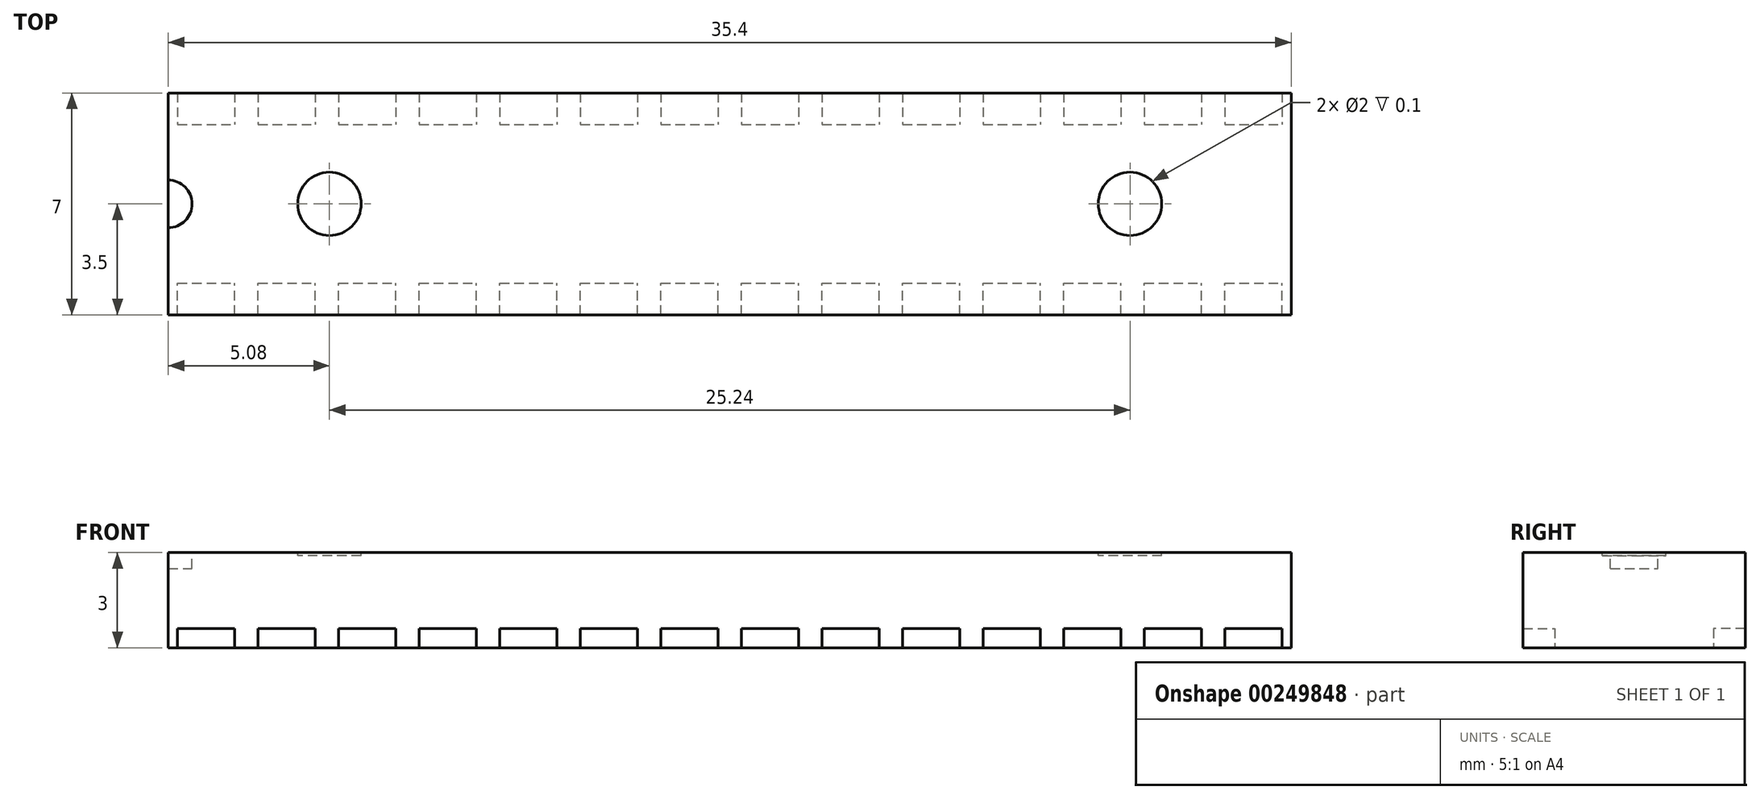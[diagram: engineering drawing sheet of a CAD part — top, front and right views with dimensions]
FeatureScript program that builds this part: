
annotation { "Feature Type Name" : "Feature", "Feature Type Description" : "" }
export const myFeature = defineFeature(function(context is Context, id is Id, definition is map)
    precondition{}
    {
        {
            var Q0;
            Q0=qCreatedBy(makeId("Top.planeOp"),FACE);
            var sketch = newSketch(context, id + "F0", { "sketchPlane" : qUnion([Q0])});
            skLineSegment(sketch, "E0.bottom", {"start": v(0, 0) * mm, "end": v(35.4, 0) * mm});
            skLineSegment(sketch, "E0.top", {"start": v(0, 7) * mm, "end": v(35.4, 7) * mm});
            skLineSegment(sketch, "E0.left", {"start": v(0, 0) * mm, "end": v(0, 7) * mm});
            skLineSegment(sketch, "E0.right", {"start": v(35.4, 0) * mm, "end": v(35.4, 7) * mm});
            skSolve(sketch);
        }
        {
            var Q0;
            Q0 = qSketchRegion(id + "F0", true);
            extrude(context, id + "F1", {"entities" : qUnion([Q0]), "depth" : 3 * mm});
        }
        {
            var Q0;
            Q0=makeQuery(id+"F1.opExtrude","CAP_FACE",FACE,{"disambiguationData":[OSD([sQuery(id+"F0.wireOp",EDGE,"E0.bottom"),sQuery(id+"F0.wireOp",EDGE,"E0.top"),sQuery(id+"F0.wireOp",EDGE,"E0.left"),sQuery(id+"F0.wireOp",EDGE,"E0.right")])],"isStart":true});
            var sketch = newSketch(context, id + "F2", { "sketchPlane" : qUnion([Q0])});
            skLineSegment(sketch, "E1", {"start": v(17.7, 0) * mm, "end": v(17.7, -7) * mm, "construction": true});
            skLineSegment(sketch, "E2.bottom", {"start": v(15.53, 0) * mm, "end": v(17.33, 0) * mm});
            skLineSegment(sketch, "E2.top", {"start": v(15.53, -1) * mm, "end": v(17.33, -1) * mm});
            skLineSegment(sketch, "E2.left", {"start": v(15.53, 0) * mm, "end": v(15.53, -1) * mm});
            skLineSegment(sketch, "E2.right", {"start": v(17.33, 0) * mm, "end": v(17.33, -1) * mm});
            skLineSegment(sketch, "E3.1.0.0", {"start": v(18.07, 0) * mm, "end": v(18.07, -1) * mm});
            skLineSegment(sketch, "E3.1.0.1", {"start": v(18.07, 0) * mm, "end": v(19.87, 0) * mm});
            skLineSegment(sketch, "E3.1.0.2", {"start": v(18.07, -1) * mm, "end": v(19.87, -1) * mm});
            skLineSegment(sketch, "E3.1.0.3", {"start": v(19.87, 0) * mm, "end": v(19.87, -1) * mm});
            skLineSegment(sketch, "E3.2.0.0", {"start": v(20.61, 0) * mm, "end": v(20.61, -1) * mm});
            skLineSegment(sketch, "E3.2.0.1", {"start": v(20.61, 0) * mm, "end": v(22.41, 0) * mm});
            skLineSegment(sketch, "E3.2.0.2", {"start": v(20.61, -1) * mm, "end": v(22.41, -1) * mm});
            skLineSegment(sketch, "E3.2.0.3", {"start": v(22.41, 0) * mm, "end": v(22.41, -1) * mm});
            skLineSegment(sketch, "E3.3.0.0", {"start": v(23.15, 0) * mm, "end": v(23.15, -1) * mm});
            skLineSegment(sketch, "E3.3.0.1", {"start": v(23.15, 0) * mm, "end": v(24.95, 0) * mm});
            skLineSegment(sketch, "E3.3.0.2", {"start": v(23.15, -1) * mm, "end": v(24.95, -1) * mm});
            skLineSegment(sketch, "E3.3.0.3", {"start": v(24.95, 0) * mm, "end": v(24.95, -1) * mm});
            skLineSegment(sketch, "E3.4.0.0", {"start": v(25.7, 0) * mm, "end": v(25.7, -1) * mm});
            skLineSegment(sketch, "E3.4.0.1", {"start": v(25.7, 0) * mm, "end": v(27.5, 0) * mm});
            skLineSegment(sketch, "E3.4.0.2", {"start": v(25.7, -1) * mm, "end": v(27.5, -1) * mm});
            skLineSegment(sketch, "E3.4.0.3", {"start": v(27.5, 0) * mm, "end": v(27.5, -1) * mm});
            skLineSegment(sketch, "E3.5.0.0", {"start": v(28.23, 0) * mm, "end": v(28.23, -1) * mm});
            skLineSegment(sketch, "E3.5.0.1", {"start": v(28.23, 0) * mm, "end": v(30.03, 0) * mm});
            skLineSegment(sketch, "E3.5.0.2", {"start": v(28.23, -1) * mm, "end": v(30.03, -1) * mm});
            skLineSegment(sketch, "E3.5.0.3", {"start": v(30.03, 0) * mm, "end": v(30.03, -1) * mm});
            skLineSegment(sketch, "E3.6.0.0", {"start": v(30.77, 0) * mm, "end": v(30.77, -1) * mm});
            skLineSegment(sketch, "E3.6.0.1", {"start": v(30.77, 0) * mm, "end": v(32.57, 0) * mm});
            skLineSegment(sketch, "E3.6.0.2", {"start": v(30.77, -1) * mm, "end": v(32.57, -1) * mm});
            skLineSegment(sketch, "E3.6.0.3", {"start": v(32.57, 0) * mm, "end": v(32.57, -1) * mm});
            skLineSegment(sketch, "E3.7.0.0", {"start": v(33.31, 0) * mm, "end": v(33.31, -1) * mm});
            skLineSegment(sketch, "E3.7.0.1", {"start": v(33.31, 0) * mm, "end": v(35.1, 0) * mm});
            skLineSegment(sketch, "E3.7.0.2", {"start": v(33.31, -1) * mm, "end": v(35.1, -1) * mm});
            skLineSegment(sketch, "E3.7.0.3", {"start": v(35.1, 0) * mm, "end": v(35.1, -1) * mm});
            skLineSegment(sketch, "E3.direction1", {"start": v(15.53, -1) * mm, "end": v(18.07, -1) * mm, "construction": true});
            skLineSegment(sketch, "E4.1.0.0", {"start": v(14.8, 0) * mm, "end": v(14.8, -1) * mm});
            skLineSegment(sketch, "E4.1.0.1", {"start": v(13, 0) * mm, "end": v(13, -1) * mm});
            skLineSegment(sketch, "E4.1.0.2", {"start": v(13, 0) * mm, "end": v(14.8, 0) * mm});
            skLineSegment(sketch, "E4.2.0.0", {"start": v(12.25, 0) * mm, "end": v(12.25, -1) * mm});
            skLineSegment(sketch, "E4.2.0.1", {"start": v(10.45, 0) * mm, "end": v(10.45, -1) * mm});
            skLineSegment(sketch, "E4.2.0.2", {"start": v(10.45, 0) * mm, "end": v(12.25, 0) * mm});
            skLineSegment(sketch, "E4.3.0.0", {"start": v(9.7, 0) * mm, "end": v(9.7, -1) * mm});
            skLineSegment(sketch, "E4.3.0.1", {"start": v(7.9, 0) * mm, "end": v(7.9, -1) * mm});
            skLineSegment(sketch, "E4.3.0.2", {"start": v(7.9, 0) * mm, "end": v(9.7, 0) * mm});
            skLineSegment(sketch, "E4.4.0.0", {"start": v(7.17, 0) * mm, "end": v(7.17, -1) * mm});
            skLineSegment(sketch, "E4.4.0.1", {"start": v(5.37, 0) * mm, "end": v(5.37, -1) * mm});
            skLineSegment(sketch, "E4.4.0.2", {"start": v(5.37, 0) * mm, "end": v(7.17, 0) * mm});
            skLineSegment(sketch, "E4.5.0.0", {"start": v(4.63, 0) * mm, "end": v(4.63, -1) * mm});
            skLineSegment(sketch, "E4.5.0.1", {"start": v(2.83, 0) * mm, "end": v(2.83, -1) * mm});
            skLineSegment(sketch, "E4.5.0.2", {"start": v(2.83, 0) * mm, "end": v(4.63, 0) * mm});
            skLineSegment(sketch, "E4.6.0.0", {"start": v(2.09, 0) * mm, "end": v(2.09, -1) * mm});
            skLineSegment(sketch, "E4.6.0.1", {"start": v(0.29, 0) * mm, "end": v(0.29, -1) * mm});
            skLineSegment(sketch, "E4.6.0.2", {"start": v(0.29, 0) * mm, "end": v(2.09, 0) * mm});
            skLineSegment(sketch, "E4.direction1", {"start": v(17.33, -1) * mm, "end": v(14.8, -1) * mm, "construction": true});
            skLineSegment(sketch, "E5", {"start": v(0.29, -1) * mm, "end": v(2.09, -1) * mm});
            skLineSegment(sketch, "E6", {"start": v(2.83, -1) * mm, "end": v(4.63, -1) * mm});
            skLineSegment(sketch, "E7", {"start": v(5.37, -1) * mm, "end": v(7.17, -1) * mm});
            skLineSegment(sketch, "E8", {"start": v(7.9, -1) * mm, "end": v(9.7, -1) * mm});
            skLineSegment(sketch, "E9", {"start": v(10.45, -1) * mm, "end": v(12.25, -1) * mm});
            skLineSegment(sketch, "E10", {"start": v(13, -1) * mm, "end": v(14.8, -1) * mm});
            skLineSegment(sketch, "E11", {"start": v(0, -3.5) * mm, "end": v(35.4, -3.5) * mm, "construction": true});
            skLineSegment(sketch, "E12.MirrorCS", {"start": v(2.09, -7) * mm, "end": v(2.09, -6) * mm});
            skLineSegment(sketch, "E13.MirrorCS", {"start": v(0.29, -7) * mm, "end": v(2.09, -7) * mm});
            skLineSegment(sketch, "E14.MirrorCS", {"start": v(0.29, -6) * mm, "end": v(2.09, -6) * mm});
            skLineSegment(sketch, "E15.MirrorCS", {"start": v(0.29, -7) * mm, "end": v(0.29, -6) * mm});
            skLineSegment(sketch, "E16.MirrorCS", {"start": v(14.8, -7) * mm, "end": v(14.8, -6) * mm});
            skLineSegment(sketch, "E17.MirrorCS", {"start": v(15.53, -6) * mm, "end": v(17.33, -6) * mm});
            skLineSegment(sketch, "E18.MirrorCS", {"start": v(7.17, -7) * mm, "end": v(7.17, -6) * mm});
            skLineSegment(sketch, "E19.MirrorCS", {"start": v(13, -7) * mm, "end": v(14.8, -7) * mm});
            skLineSegment(sketch, "E20.MirrorCS", {"start": v(2.83, -6) * mm, "end": v(4.63, -6) * mm});
            skLineSegment(sketch, "E21.MirrorCS", {"start": v(2.83, -7) * mm, "end": v(4.63, -7) * mm});
            skLineSegment(sketch, "E22.MirrorCS", {"start": v(5.37, -6) * mm, "end": v(7.17, -6) * mm});
            skLineSegment(sketch, "E23.MirrorCS", {"start": v(10.45, -7) * mm, "end": v(12.25, -7) * mm});
            skLineSegment(sketch, "E24.MirrorCS", {"start": v(17.33, -6) * mm, "end": v(14.8, -6) * mm, "construction": true});
            skLineSegment(sketch, "E25.MirrorCS", {"start": v(5.37, -7) * mm, "end": v(7.17, -7) * mm});
            skLineSegment(sketch, "E26.MirrorCS", {"start": v(5.37, -7) * mm, "end": v(5.37, -6) * mm});
            skLineSegment(sketch, "E27.MirrorCS", {"start": v(12.25, -7) * mm, "end": v(12.25, -6) * mm});
            skLineSegment(sketch, "E28.MirrorCS", {"start": v(7.9, -6) * mm, "end": v(9.7, -6) * mm});
            skLineSegment(sketch, "E29.MirrorCS", {"start": v(9.7, -7) * mm, "end": v(9.7, -6) * mm});
            skLineSegment(sketch, "E30.MirrorCS", {"start": v(4.63, -7) * mm, "end": v(4.63, -6) * mm});
            skLineSegment(sketch, "E31.MirrorCS", {"start": v(13, -6) * mm, "end": v(14.8, -6) * mm});
            skLineSegment(sketch, "E32.MirrorCS", {"start": v(13, -7) * mm, "end": v(13, -6) * mm});
            skLineSegment(sketch, "E33.MirrorCS", {"start": v(7.9, -7) * mm, "end": v(9.7, -7) * mm});
            skLineSegment(sketch, "E34.MirrorCS", {"start": v(2.83, -7) * mm, "end": v(2.83, -6) * mm});
            skLineSegment(sketch, "E35.MirrorCS", {"start": v(10.45, -7) * mm, "end": v(10.45, -6) * mm});
            skLineSegment(sketch, "E36.MirrorCS", {"start": v(7.9, -7) * mm, "end": v(7.9, -6) * mm});
            skLineSegment(sketch, "E37.MirrorCS", {"start": v(10.45, -6) * mm, "end": v(12.25, -6) * mm});
            skLineSegment(sketch, "E38.MirrorCS", {"start": v(17.33, -7) * mm, "end": v(17.33, -6) * mm});
            skLineSegment(sketch, "E39.MirrorCS", {"start": v(15.53, -7) * mm, "end": v(15.53, -6) * mm});
            skLineSegment(sketch, "E40.MirrorCS", {"start": v(15.53, -7) * mm, "end": v(17.33, -7) * mm});
            skLineSegment(sketch, "E41.MirrorCS", {"start": v(25.7, -6) * mm, "end": v(27.5, -6) * mm});
            skLineSegment(sketch, "E42.MirrorCS", {"start": v(30.77, -7) * mm, "end": v(32.57, -7) * mm});
            skLineSegment(sketch, "E43.MirrorCS", {"start": v(25.7, -7) * mm, "end": v(27.5, -7) * mm});
            skLineSegment(sketch, "E44.MirrorCS", {"start": v(22.41, -7) * mm, "end": v(22.41, -6) * mm});
            skLineSegment(sketch, "E45.MirrorCS", {"start": v(30.77, -7) * mm, "end": v(30.77, -6) * mm});
            skLineSegment(sketch, "E46.MirrorCS", {"start": v(30.77, -6) * mm, "end": v(32.57, -6) * mm});
            skLineSegment(sketch, "E47.MirrorCS", {"start": v(20.61, -6) * mm, "end": v(22.41, -6) * mm});
            skLineSegment(sketch, "E48.MirrorCS", {"start": v(33.31, -7) * mm, "end": v(33.31, -6) * mm});
            skLineSegment(sketch, "E49.MirrorCS", {"start": v(20.61, -7) * mm, "end": v(22.41, -7) * mm});
            skLineSegment(sketch, "E50.MirrorCS", {"start": v(27.5, -7) * mm, "end": v(27.5, -6) * mm});
            skLineSegment(sketch, "E51.MirrorCS", {"start": v(20.61, -7) * mm, "end": v(20.61, -6) * mm});
            skLineSegment(sketch, "E52.MirrorCS", {"start": v(19.87, -7) * mm, "end": v(19.87, -6) * mm});
            skLineSegment(sketch, "E53.MirrorCS", {"start": v(18.07, -6) * mm, "end": v(19.87, -6) * mm});
            skLineSegment(sketch, "E54.MirrorCS", {"start": v(18.07, -7) * mm, "end": v(19.87, -7) * mm});
            skLineSegment(sketch, "E55.MirrorCS", {"start": v(18.07, -7) * mm, "end": v(18.07, -6) * mm});
            skLineSegment(sketch, "E56.MirrorCS", {"start": v(24.95, -7) * mm, "end": v(24.95, -6) * mm});
            skLineSegment(sketch, "E57.MirrorCS", {"start": v(35.1, -7) * mm, "end": v(35.1, -6) * mm});
            skLineSegment(sketch, "E58.MirrorCS", {"start": v(23.15, -6) * mm, "end": v(24.95, -6) * mm});
            skLineSegment(sketch, "E59.MirrorCS", {"start": v(23.15, -7) * mm, "end": v(24.95, -7) * mm});
            skLineSegment(sketch, "E60.MirrorCS", {"start": v(23.15, -7) * mm, "end": v(23.15, -6) * mm});
            skLineSegment(sketch, "E61.MirrorCS", {"start": v(32.57, -7) * mm, "end": v(32.57, -6) * mm});
            skLineSegment(sketch, "E62.MirrorCS", {"start": v(33.31, -7) * mm, "end": v(35.1, -7) * mm});
            skLineSegment(sketch, "E63.MirrorCS", {"start": v(30.03, -7) * mm, "end": v(30.03, -6) * mm});
            skLineSegment(sketch, "E64.MirrorCS", {"start": v(28.23, -7) * mm, "end": v(28.23, -6) * mm});
            skLineSegment(sketch, "E65.MirrorCS", {"start": v(33.31, -6) * mm, "end": v(35.1, -6) * mm});
            skLineSegment(sketch, "E66.MirrorCS", {"start": v(28.23, -7) * mm, "end": v(30.03, -7) * mm});
            skLineSegment(sketch, "E67.MirrorCS", {"start": v(25.7, -7) * mm, "end": v(25.7, -6) * mm});
            skLineSegment(sketch, "E68.MirrorCS", {"start": v(28.23, -6) * mm, "end": v(30.03, -6) * mm});
            skSolve(sketch);
        }
        {
            var Q0;
            Q0=makeQuery(id+"F2.imprint","IMPRINT",FACE,{"disambiguationData":[TD([[makeQuery(id+"F2.imprint","IMPRINT",EDGE,{"derivedFrom":sQuery(id+"F2.wireOp",EDGE,"E4.6.0.0")}),-1.0]])]});
            var Q1;
            Q1=makeQuery(id+"F2.imprint","IMPRINT",FACE,{"disambiguationData":[TD([[makeQuery(id+"F2.imprint","IMPRINT",EDGE,{"derivedFrom":sQuery(id+"F2.wireOp",EDGE,"E4.5.0.0")}),-1.0]])]});
            var Q2;
            Q2=makeQuery(id+"F2.imprint","IMPRINT",FACE,{"disambiguationData":[TD([[makeQuery(id+"F2.imprint","IMPRINT",EDGE,{"derivedFrom":sQuery(id+"F2.wireOp",EDGE,"E4.4.0.0")}),-1.0]])]});
            var Q3;
            Q3=makeQuery(id+"F2.imprint","IMPRINT",FACE,{"disambiguationData":[TD([[makeQuery(id+"F2.imprint","IMPRINT",EDGE,{"derivedFrom":sQuery(id+"F2.wireOp",EDGE,"E4.3.0.0")}),-1.0]])]});
            var Q4;
            Q4=makeQuery(id+"F2.imprint","IMPRINT",FACE,{"disambiguationData":[TD([[makeQuery(id+"F2.imprint","IMPRINT",EDGE,{"derivedFrom":sQuery(id+"F2.wireOp",EDGE,"E4.2.0.0")}),-1.0]])]});
            var Q5;
            Q5=makeQuery(id+"F2.imprint","IMPRINT",FACE,{"disambiguationData":[TD([[makeQuery(id+"F2.imprint","IMPRINT",EDGE,{"derivedFrom":sQuery(id+"F2.wireOp",EDGE,"E4.1.0.0")}),-1.0]])]});
            var Q6;
            Q6=makeQuery(id+"F2.imprint","IMPRINT",FACE,{"disambiguationData":[TD([[makeQuery(id+"F2.imprint","IMPRINT",EDGE,{"derivedFrom":sQuery(id+"F2.wireOp",EDGE,"E2.bottom")}),-1.0]])]});
            var Q7;
            Q7=makeQuery(id+"F2.imprint","IMPRINT",FACE,{"disambiguationData":[TD([[makeQuery(id+"F2.imprint","IMPRINT",EDGE,{"derivedFrom":sQuery(id+"F2.wireOp",EDGE,"E3.1.0.0")}),1.0]])]});
            var Q8;
            Q8=makeQuery(id+"F2.imprint","IMPRINT",FACE,{"disambiguationData":[TD([[makeQuery(id+"F2.imprint","IMPRINT",EDGE,{"derivedFrom":sQuery(id+"F2.wireOp",EDGE,"E3.2.0.0")}),1.0]])]});
            var Q9;
            Q9=makeQuery(id+"F2.imprint","IMPRINT",FACE,{"disambiguationData":[TD([[makeQuery(id+"F2.imprint","IMPRINT",EDGE,{"derivedFrom":sQuery(id+"F2.wireOp",EDGE,"E3.3.0.0")}),1.0]])]});
            var Q10;
            Q10=makeQuery(id+"F2.imprint","IMPRINT",FACE,{"disambiguationData":[TD([[makeQuery(id+"F2.imprint","IMPRINT",EDGE,{"derivedFrom":sQuery(id+"F2.wireOp",EDGE,"E3.4.0.0")}),1.0]])]});
            var Q11;
            Q11=makeQuery(id+"F2.imprint","IMPRINT",FACE,{"disambiguationData":[TD([[makeQuery(id+"F2.imprint","IMPRINT",EDGE,{"derivedFrom":sQuery(id+"F2.wireOp",EDGE,"E3.5.0.0")}),1.0]])]});
            var Q12;
            Q12=makeQuery(id+"F2.imprint","IMPRINT",FACE,{"disambiguationData":[TD([[makeQuery(id+"F2.imprint","IMPRINT",EDGE,{"derivedFrom":sQuery(id+"F2.wireOp",EDGE,"E3.6.0.0")}),1.0]])]});
            var Q13;
            Q13=makeQuery(id+"F2.imprint","IMPRINT",FACE,{"disambiguationData":[TD([[makeQuery(id+"F2.imprint","IMPRINT",EDGE,{"derivedFrom":sQuery(id+"F2.wireOp",EDGE,"E3.7.0.0")}),1.0]])]});
            var Q14;
            Q14=makeQuery(id+"F2.imprint","IMPRINT",FACE,{"disambiguationData":[TD([[makeQuery(id+"F2.imprint","IMPRINT",EDGE,{"derivedFrom":sQuery(id+"F2.wireOp",EDGE,"E48.MirrorCS")}),-1.0]])]});
            var Q15;
            Q15=makeQuery(id+"F2.imprint","IMPRINT",FACE,{"disambiguationData":[TD([[makeQuery(id+"F2.imprint","IMPRINT",EDGE,{"derivedFrom":sQuery(id+"F2.wireOp",EDGE,"E42.MirrorCS")}),1.0]])]});
            var Q16;
            Q16=makeQuery(id+"F2.imprint","IMPRINT",FACE,{"disambiguationData":[TD([[makeQuery(id+"F2.imprint","IMPRINT",EDGE,{"derivedFrom":sQuery(id+"F2.wireOp",EDGE,"E63.MirrorCS")}),1.0]])]});
            var Q17;
            Q17=makeQuery(id+"F2.imprint","IMPRINT",FACE,{"disambiguationData":[TD([[makeQuery(id+"F2.imprint","IMPRINT",EDGE,{"derivedFrom":sQuery(id+"F2.wireOp",EDGE,"E41.MirrorCS")}),-1.0]])]});
            var Q18;
            Q18=makeQuery(id+"F2.imprint","IMPRINT",FACE,{"disambiguationData":[TD([[makeQuery(id+"F2.imprint","IMPRINT",EDGE,{"derivedFrom":sQuery(id+"F2.wireOp",EDGE,"E56.MirrorCS")}),1.0]])]});
            var Q19;
            Q19=makeQuery(id+"F2.imprint","IMPRINT",FACE,{"disambiguationData":[TD([[makeQuery(id+"F2.imprint","IMPRINT",EDGE,{"derivedFrom":sQuery(id+"F2.wireOp",EDGE,"E44.MirrorCS")}),1.0]])]});
            var Q20;
            Q20=makeQuery(id+"F2.imprint","IMPRINT",FACE,{"disambiguationData":[TD([[makeQuery(id+"F2.imprint","IMPRINT",EDGE,{"derivedFrom":sQuery(id+"F2.wireOp",EDGE,"E52.MirrorCS")}),1.0]])]});
            var Q21;
            Q21=makeQuery(id+"F2.imprint","IMPRINT",FACE,{"disambiguationData":[TD([[makeQuery(id+"F2.imprint","IMPRINT",EDGE,{"derivedFrom":sQuery(id+"F2.wireOp",EDGE,"E17.MirrorCS")}),-1.0]])]});
            var Q22;
            Q22=makeQuery(id+"F2.imprint","IMPRINT",FACE,{"disambiguationData":[TD([[makeQuery(id+"F2.imprint","IMPRINT",EDGE,{"derivedFrom":sQuery(id+"F2.wireOp",EDGE,"E16.MirrorCS")}),1.0]])]});
            var Q23;
            Q23=makeQuery(id+"F2.imprint","IMPRINT",FACE,{"disambiguationData":[TD([[makeQuery(id+"F2.imprint","IMPRINT",EDGE,{"derivedFrom":sQuery(id+"F2.wireOp",EDGE,"E23.MirrorCS")}),1.0]])]});
            var Q24;
            Q24=makeQuery(id+"F2.imprint","IMPRINT",FACE,{"disambiguationData":[TD([[makeQuery(id+"F2.imprint","IMPRINT",EDGE,{"derivedFrom":sQuery(id+"F2.wireOp",EDGE,"E28.MirrorCS")}),-1.0]])]});
            var Q25;
            Q25=makeQuery(id+"F2.imprint","IMPRINT",FACE,{"disambiguationData":[TD([[makeQuery(id+"F2.imprint","IMPRINT",EDGE,{"derivedFrom":sQuery(id+"F2.wireOp",EDGE,"E18.MirrorCS")}),1.0]])]});
            var Q26;
            Q26=makeQuery(id+"F2.imprint","IMPRINT",FACE,{"disambiguationData":[TD([[makeQuery(id+"F2.imprint","IMPRINT",EDGE,{"derivedFrom":sQuery(id+"F2.wireOp",EDGE,"E20.MirrorCS")}),-1.0]])]});
            var Q27;
            Q27=makeQuery(id+"F2.imprint","IMPRINT",FACE,{"disambiguationData":[TD([[makeQuery(id+"F2.imprint","IMPRINT",EDGE,{"derivedFrom":sQuery(id+"F2.wireOp",EDGE,"E12.MirrorCS")}),1.0]])]});
            extrude(context, id + "F3", {"entities" : qUnion([Q0, Q1, Q2, Q3, Q4, Q5, Q6, Q7, Q8, Q9, Q10, Q11, Q12, Q13, Q14, Q15, Q16, Q17, Q18, Q19, Q20, Q21, Q22, Q23, Q24, Q25, Q26, Q27]), "operationType" : NewBodyOperationType.REMOVE, "oppositeDirection" : true, "depth" : 0.6 * mm});
        }
        {
            var Q0;
            Q0=makeQuery(id+"F1.opExtrude","CAP_FACE",FACE,{"disambiguationData":[OSD([sQuery(id+"F0.wireOp",EDGE,"E0.bottom"),sQuery(id+"F0.wireOp",EDGE,"E0.top"),sQuery(id+"F0.wireOp",EDGE,"E0.left"),sQuery(id+"F0.wireOp",EDGE,"E0.right")])],"isStart":false});
            var sketch = newSketch(context, id + "F4", { "sketchPlane" : qUnion([Q0])});
            skLineSegment(sketch, "E69", {"start": v(0, 3.5) * mm, "end": v(35.4, 3.5) * mm, "construction": true});
            skCircle(sketch, "E70", {"center": v(5.08, 3.5) * mm, "radius": 1 * mm});
            skCircle(sketch, "E71", {"center": v(30.32, 3.5) * mm, "radius": 1 * mm});
            skSolve(sketch);
        }
        {
            var Q0;
            Q0 = qSketchRegion(id + "F4", true);
            extrude(context, id + "F5", {"entities" : qUnion([Q0]), "operationType" : NewBodyOperationType.REMOVE, "oppositeDirection" : true, "depth" : 0.1 * mm});
        }
        {
            var Q0;
            Q0=makeQuery(id+"F1.opExtrude","CAP_FACE",FACE,{"disambiguationData":[OSD([sQuery(id+"F0.wireOp",EDGE,"E0.bottom"),sQuery(id+"F0.wireOp",EDGE,"E0.top"),sQuery(id+"F0.wireOp",EDGE,"E0.left"),sQuery(id+"F0.wireOp",EDGE,"E0.right")])],"isStart":false});
            var sketch = newSketch(context, id + "F6", { "sketchPlane" : qUnion([Q0])});
            skArc(sketch, "E72", {"start": v(0, 2.75) * mm, "mid": v(0.75, 3.5) * mm, "end": v(0, 4.25) * mm});
            skLineSegment(sketch, "E73", {"start": v(0, 4.25) * mm, "end": v(0, 2.75) * mm});
            skSolve(sketch);
        }
        {
            var Q0;
            Q0 = qSketchRegion(id + "F6", true);
            extrude(context, id + "F7", {"entities" : qUnion([Q0]), "operationType" : NewBodyOperationType.REMOVE, "oppositeDirection" : true, "depth" : 0.5 * mm});
        }
    });
